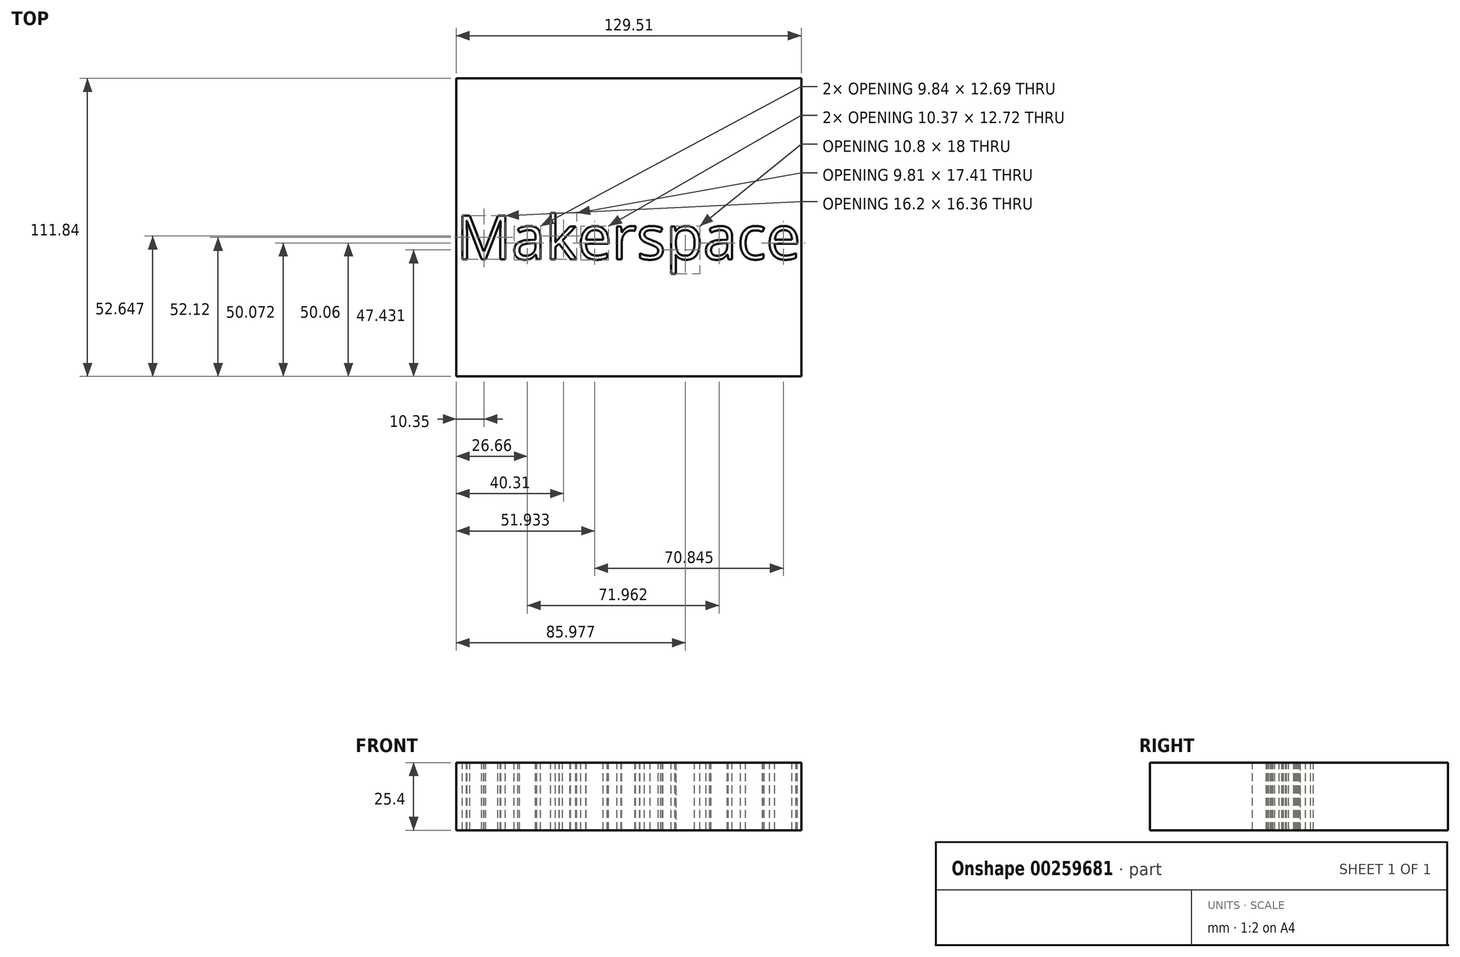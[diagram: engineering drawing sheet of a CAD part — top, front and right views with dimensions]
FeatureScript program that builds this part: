
annotation { "Feature Type Name" : "Feature", "Feature Type Description" : "" }
export const myFeature = defineFeature(function(context is Context, id is Id, definition is map)
    precondition{}
    {
        {
            var Q0;
            Q0=qCreatedBy(makeId("Top.planeOp"),FACE);
            var sketch = newSketch(context, id + "F0", { "sketchPlane" : qUnion([Q0])});
            skLineSegment(sketch, "E0.bottom", {"start": v(-57.26, -50.56) * mm, "end": v(72.25, -50.56) * mm});
            skLineSegment(sketch, "E0.top", {"start": v(-57.26, 61.28) * mm, "end": v(72.25, 61.28) * mm});
            skLineSegment(sketch, "E0.left", {"start": v(-57.26, -50.56) * mm, "end": v(-57.26, 61.28) * mm});
            skLineSegment(sketch, "E0.right", {"start": v(72.25, -50.56) * mm, "end": v(72.25, 61.28) * mm});
            skSolve(sketch);
        }
        {
            var Q0;
            Q0=makeQuery(id+"F0.imprint","IMPRINT",FACE,{"disambiguationData":[TD([[makeQuery(id+"F0.imprint","IMPRINT",EDGE,{"derivedFrom":sQuery(id+"F0.wireOp",EDGE,"E0.bottom")}),1.0]])]});
            extrude(context, id + "F1", {"entities" : qUnion([Q0]), "depth" : 25.4 * mm});
        }
        {
            var Q0;
            Q0=makeQuery(id+"F1.opExtrude","CAP_FACE",FACE,{"disambiguationData":[OSD([sQuery(id+"F0.wireOp",EDGE,"E0.bottom"),sQuery(id+"F0.wireOp",EDGE,"E0.top"),sQuery(id+"F0.wireOp",EDGE,"E0.left"),sQuery(id+"F0.wireOp",EDGE,"E0.right")])],"isStart":false});
            var sketch = newSketch(context, id + "F2", { "sketchPlane" : qUnion([Q0])});
            skText(sketch, "E1", { "text": "Makerspace", "fontName": "OpenSans-Regular.ttf"});
            const initialGuessF2  = {"E1": [-0.05726, -0.00662, 1, 0, 0.0165]};
            skSetInitialGuess(sketch, initialGuessF2);
            skSolve(sketch);
        }
        {
            var Q0;
            Q0 = qSketchRegion(id + "F2", true);
            extrude(context, id + "F3", {"entities" : qUnion([Q0]), "operationType" : NewBodyOperationType.REMOVE, "oppositeDirection" : true, "depth" : 25.4 * mm});
        }
    });
